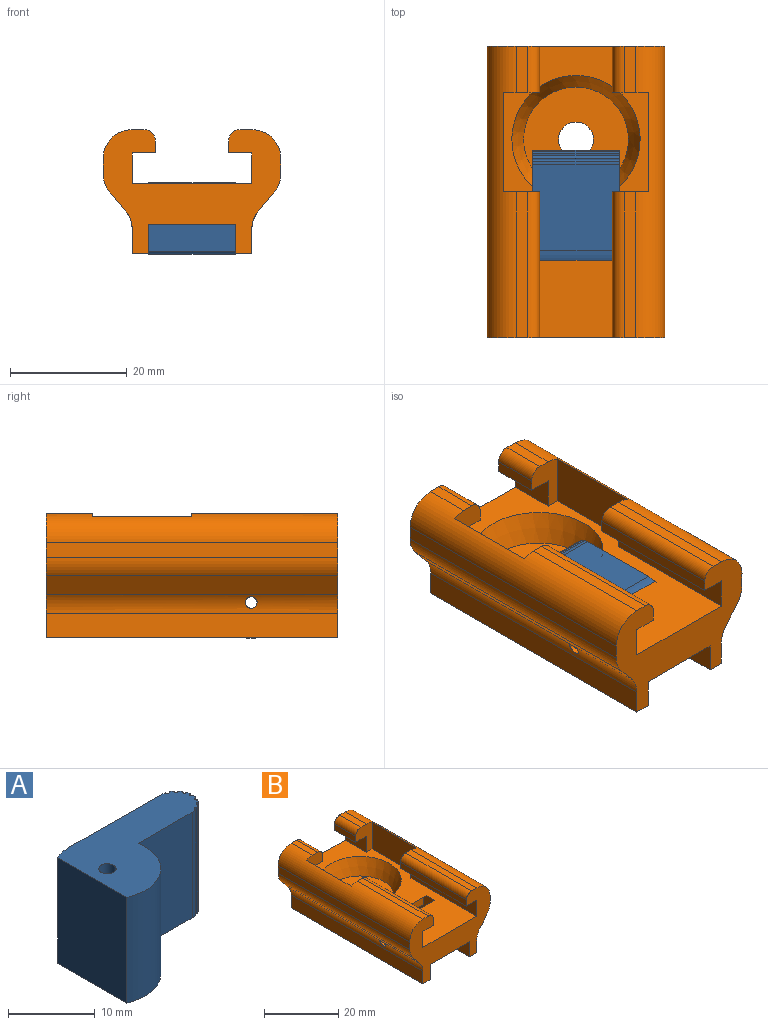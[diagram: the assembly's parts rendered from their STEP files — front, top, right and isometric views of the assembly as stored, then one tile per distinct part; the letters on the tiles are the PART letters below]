
ASSEMBLY  parts=2 mates=1
PART A: 23 faces, bbox 19.8x12.3x14.9 mm
  f0: cylinder r=0.25mm len=14.9mm, axis (0,0,-1), area 11.3mm2, adj f1,f19,f20,f21
  f1: cylinder r=2.5mm len=14.9mm, axis (0,0,-1), area 7.7mm2, adj f0,f2,f20,f21
  f2: cylinder r=0.25mm len=14.9mm, axis (0,0,-1), area 11.3mm2, adj f1,f3,f20,f21
  f3: cylinder r=2.5mm len=14.9mm, axis (0,0,-1), area 8.5mm2, adj f2,f4,f20,f21
  f4: plane 14.9x14.84mm, normal (0.01,1,0), area 221.2mm2, adj f3,f5,f20,f21
  f5: cylinder r=6.15mm len=14.9mm, axis (0,0,-1), area 38.7mm2, adj f4,f6,f20,f21
  f6: plane 14.9x11.25mm, normal (-1,0,0), area 167.7mm2, adj f5,f7,f20,f21
  f7: cylinder r=6.15mm len=14.9mm, axis (0,0,-1), area 197.8mm2, adj f6,f8,f20,f21
  f8: plane 14.9x8.79mm, normal (0,-1,0), area 131mm2, adj f7,f9,f20,f21
  f9: cylinder r=2.5mm len=14.9mm, axis (0,0,-1), area 9.5mm2, adj f8,f10,f20,f21
  f10: cylinder r=0.25mm len=14.9mm, axis (0,0,-1), area 11.3mm2, adj f9,f11,f20,f21
  f11: cylinder r=2.5mm len=14.9mm, axis (0,0,-1), area 7.7mm2, adj f10,f12,f20,f21
  f12: cylinder r=0.25mm len=14.9mm, axis (0,0,-1), area 11.3mm2, adj f11,f13,f20,f21
  f13: cylinder r=2.5mm len=14.9mm, axis (0,0,-1), area 7.7mm2, adj f12,f14,f20,f21
  f14: cylinder r=0.25mm len=14.9mm, axis (0,0,-1), area 11.3mm2, adj f13,f15,f20,f21
  f15: cylinder r=2.5mm len=14.9mm, axis (0,0,-1), area 7.7mm2, adj f14,f16,f20,f21
  f16: cylinder r=0.25mm len=14.9mm, axis (0,0,-1), area 11.3mm2, adj f15,f17,f20,f21
  f17: cylinder r=2.5mm len=14.9mm, axis (0,0,-1), area 7.7mm2, adj f16,f18,f20,f21
  f18: cylinder r=0.25mm len=14.9mm, axis (0,0,-1), area 11.3mm2, adj f17,f19,f20,f21
  f19: cylinder r=2.5mm len=14.9mm, axis (0,0,-1), area 7.7mm2, adj f0,f18,f20,f21
  f20: plane 19.82x12.3mm, normal (0,0,1), area 146.8mm2, adj f0,f1,f2,f3,f4,f5,f6,f7
  f21: plane 19.82x12.3mm, normal (0,0,-1), area 146.8mm2, adj f0,f1,f2,f3,f4,f5,f6,f7
  f22: cylinder r=1mm len=14.9mm, axis (0,0,1), area 93.6mm2, adj f20,f21
PART B: 60 faces, bbox 30.5x50x21.3 mm
  f0: plane 5x0.05mm, normal (0,-1,0), area 0.2mm2, adj f4,f5,f47,f51
  f1: plane 14.9x3.14mm, normal (0,-1,0), area 46.8mm2, adj f48,f50,f51,f56
  f2: cylinder r=5mm len=50mm, axis (0,-1,0), area 170.3mm2, adj f18,f19,f37,f38,f53
  f3: cylinder r=5mm len=50mm, axis (0,-1,0), area 170.3mm2, adj f20,f21,f37,f38,f52
  f4: plane 20x15mm, normal (0,0,-1), area 133mm2, adj f0,f38,f45,f46,f47,f49,f50,f51
  f5: plane 50x20.5mm, normal (0,0,-1), area 682.4mm2, adj f0,f19,f20,f37,f38,f45,f46,f47
  f6: plane 25x2mm, normal (0,0,1), area 50mm2, adj f7,f24,f38,f44
  f7: cylinder r=2mm len=25mm, axis (0,-1,0), area 78.5mm2, adj f6,f8,f38,f44
  f8: plane 25x2mm, normal (1,0,0), area 50mm2, adj f7,f9,f38,f44
  f9: plane 25x4mm, normal (0,0,-1), area 100mm2, adj f8,f10,f38,f44
  f10: plane 25x5.3mm, normal (1,0,0), area 132.5mm2, adj f9,f30,f38,f44
  f11: plane 25x5.3mm, normal (-1,0,0), area 132.5mm2, adj f12,f30,f38,f40
  f12: plane 25x4mm, normal (0,0,-1), area 100mm2, adj f11,f13,f38,f40
  f13: plane 25x2mm, normal (-1,0,0), area 50mm2, adj f12,f14,f38,f40
  f14: cylinder r=2mm len=25mm, axis (0,-1,0), area 78.5mm2, adj f13,f15,f38,f40
  f15: plane 25x2mm, normal (0,0,1), area 50mm2, adj f14,f36,f38,f40
  f16: plane 50x2.49mm, normal (1,0,0), area 124.5mm2, adj f17,f36,f37,f38
  f17: cylinder r=5mm len=50mm, axis (0,-1,0), area 173.7mm2, adj f16,f18,f37,f38
  f18: plane 50x3.22mm, normal (0.77,0,-0.64), area 209.5mm2, adj f2,f17,f37,f38
  f19: plane 50x4.19mm, normal (1,0,0), area 209.5mm2, adj f2,f5,f37,f38
  f20: plane 50x4.19mm, normal (-1,0,0), area 209.5mm2, adj f3,f5,f37,f38
  f21: plane 50x3.22mm, normal (-0.77,0,-0.64), area 209.5mm2, adj f3,f22,f37,f38
  f22: cylinder r=5mm len=50mm, axis (0,-1,0), area 173.7mm2, adj f21,f23,f37,f38
  f23: plane 50x2.49mm, normal (-1,0,0), area 124.5mm2, adj f22,f24,f37,f38
  f24: cylinder r=5mm len=50mm, axis (0,-1,0), area 353mm2, adj f6,f23,f25,f37,f38,f42,f43,f44
  f25: plane 8x2mm, normal (0,0,1), area 16mm2, adj f24,f26,f37,f43
  f26: cylinder r=2mm len=8mm, axis (0,-1,0), area 25.1mm2, adj f25,f27,f37,f43
  f27: plane 8x2mm, normal (1,0,0), area 16mm2, adj f26,f28,f37,f43
  f28: plane 8x4mm, normal (0,0,-1), area 32mm2, adj f27,f29,f37,f43
  f29: plane 8x5.3mm, normal (1,0,0), area 42.4mm2, adj f28,f30,f37,f43
  f30: plane 50x25mm, normal (0,0,1), area 674.4mm2, adj f10,f11,f29,f31,f37,f38,f39,f40
  f31: plane 8x5.3mm, normal (-1,0,0), area 42.4mm2, adj f30,f32,f37,f41
  f32: plane 8x4mm, normal (0,0,-1), area 32mm2, adj f31,f33,f37,f41
  f33: plane 8x2mm, normal (-1,0,0), area 16mm2, adj f32,f34,f37,f41
  f34: cylinder r=2mm len=8mm, axis (0,-1,0), area 25.1mm2, adj f33,f35,f37,f41
  f35: plane 8x2mm, normal (0,0,1), area 16mm2, adj f34,f36,f37,f41
  f36: cylinder r=5mm len=50mm, axis (0,-1,0), area 353mm2, adj f15,f16,f35,f37,f38,f39,f40,f41
  f37: plane 30.5x21.3mm, normal (0,1,0), area 388.6mm2, adj f2,f3,f5,f16,f17,f18,f19,f20
  f38: plane 30.5x21.3mm, normal (0,-1,0), area 313.6mm2, adj f2,f3,f4,f5,f6,f7,f8,f9
  f39: plane 17x8.77mm, normal (-1,0,0), area 149mm2, adj f30,f36,f40,f41
  f40: plane 9.3x6.25mm, normal (0,1,0), area 35.7mm2, adj f11,f12,f13,f14,f15,f30,f36,f39
  f41: plane 9.3x6.25mm, normal (0,-1,0), area 35.7mm2, adj f30,f31,f32,f33,f34,f35,f36,f39
  f42: plane 17x8.77mm, normal (1,0,0), area 149mm2, adj f24,f30,f43,f44
  f43: plane 9.3x6.25mm, normal (0,-1,0), area 35.7mm2, adj f24,f25,f26,f27,f28,f29,f30,f42
  f44: plane 9.3x6.25mm, normal (0,1,0), area 35.7mm2, adj f6,f7,f8,f9,f10,f24,f30,f42
  f45: plane 5x0.05mm, normal (0,-1,0), area 0.2mm2, adj f4,f5,f46,f50
  f46: plane 20x5mm, normal (-1,0,0), area 100mm2, adj f4,f5,f38,f45
  f47: plane 20x5mm, normal (1,0,0), area 100mm2, adj f0,f4,f5,f38
  f48: cylinder r=6.15mm len=14.9mm, axis (-1,0,0), area 14.3mm2, adj f1,f30,f50,f51
  f49: cylinder r=6.15mm len=14.9mm, axis (-1,0,0), area 136mm2, adj f4,f30,f50,f51
  f50: plane 12.3x12mm, normal (-1,0,0), area 67.5mm2, adj f1,f4,f5,f30,f45,f48,f49,f53
  f51: plane 12.3x12mm, normal (1,0,0), area 67.5mm2, adj f0,f1,f4,f5,f30,f48,f49,f52
  f52: cylinder r=1mm len=3.7mm, axis (-1,0,0), area 20.3mm2, adj f3,f51
  f53: cylinder r=1mm len=3.7mm, axis (-1,0,0), area 20.3mm2, adj f2,f50
  f54: plane 14.9x6.02mm, normal (0,-1,0.01), area 89.6mm2, adj f5,f50,f51,f55
  f55: cylinder r=6.15mm len=14.9mm, axis (-1,0,0), area 38.7mm2, adj f50,f51,f54,f56
  f56: plane 14.9x3.14mm, normal (0,0,-1), area 46.8mm2, adj f1,f50,f51,f55
  f57: plane 18x18mm, normal (0,0,1), area 226.2mm2, adj f58,f59
  f58: cylinder r=3mm len=7mm, axis (0,0,1), area 131.9mm2, adj f5,f57
  f59: cone r=9mm half-angle=21.8deg, axis (0,0,1), area 338.4mm2, adj f30,f57
PLACE A rot(axis=(0.58,0.58,0.58),120deg) t=(-24.75,40.4,1.92)mm
PLACE B t=(0.03,5.93,4.46)mm fixed
MATE cylindrical A.f5 <-> B.f48  axis (1,0,0) through (-7.42,35.43,10.52)mm
